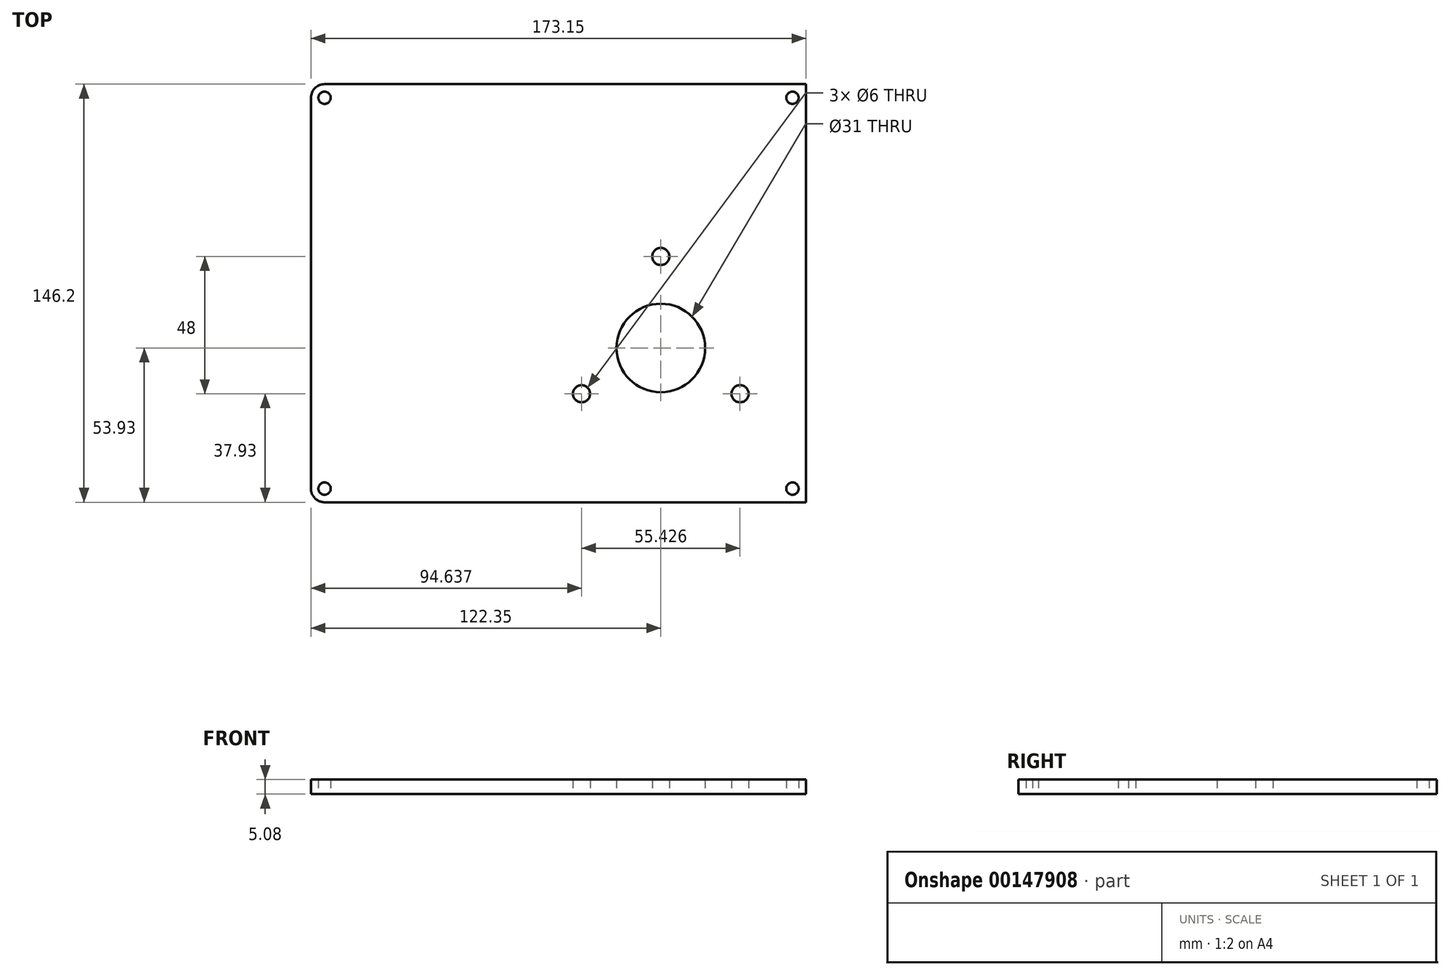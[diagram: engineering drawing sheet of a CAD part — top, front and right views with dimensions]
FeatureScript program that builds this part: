
annotation { "Feature Type Name" : "Feature", "Feature Type Description" : "" }
export const myFeature = defineFeature(function(context is Context, id is Id, definition is map)
    precondition{}
    {
        {
            var Q0;
            Q0=qCreatedBy(makeId("Top.planeOp"),FACE);
            var sketch = newSketch(context, id + "F0", { "sketchPlane" : qUnion([Q0])});
            skLineSegment(sketch, "E0", {"start": v(0, 0) * mm, "end": v(0, 32) * mm, "construction": true});
            skLineSegment(sketch, "E1", {"start": v(0, 0) * mm, "end": v(27.71, -16) * mm, "construction": true});
            skLineSegment(sketch, "E2", {"start": v(0, 0) * mm, "end": v(-27.71, -16) * mm, "construction": true});
            skLineSegment(sketch, "E3", {"start": v(0, 32) * mm, "end": v(27.71, -16) * mm, "construction": true});
            skLineSegment(sketch, "E4", {"start": v(27.71, -16) * mm, "end": v(-27.71, -16) * mm, "construction": true});
            skLineSegment(sketch, "E5", {"start": v(-27.71, -16) * mm, "end": v(0, 32) * mm, "construction": true});
            skCircle(sketch, "E6", {"center": v(0, 0) * mm, "radius": 15.5 * mm});
            skCircle(sketch, "E7", {"center": v(0, 32) * mm, "radius": 3 * mm});
            skCircle(sketch, "E8", {"center": v(-27.71, -16) * mm, "radius": 3 * mm});
            skCircle(sketch, "E9", {"center": v(27.71, -16) * mm, "radius": 3 * mm});
            skLineSegment(sketch, "E10.bottom", {"start": v(-117.58, 92.27) * mm, "end": v(50.8, 92.27) * mm});
            skLineSegment(sketch, "E10.top", {"start": v(-117.58, -53.93) * mm, "end": v(50.8, -53.93) * mm});
            skLineSegment(sketch, "E10.right", {"start": v(50.8, 92.27) * mm, "end": v(50.8, -53.93) * mm});
            skLineSegment(sketch, "E11", {"start": v(50.8, -49.17) * mm, "end": v(46.04, -49.17) * mm, "construction": true});
            skLineSegment(sketch, "E12", {"start": v(46.04, -49.17) * mm, "end": v(46.04, -53.93) * mm, "construction": true});
            skLineSegment(sketch, "E13", {"start": v(50.8, 87.51) * mm, "end": v(46.04, 87.51) * mm, "construction": true});
            skLineSegment(sketch, "E14", {"start": v(46.04, 87.51) * mm, "end": v(46.04, 92.27) * mm, "construction": true});
            skCircle(sketch, "E15", {"center": v(46.04, 87.51) * mm, "radius": 2.15 * mm});
            skCircle(sketch, "E16", {"center": v(46.04, -49.17) * mm, "radius": 2.15 * mm});
            skArc(sketch, "E17", {"start": v(-117.58, 92.27) * mm, "mid": v(-120.95, 90.88) * mm, "end": v(-122.35, 87.51) * mm});
            skArc(sketch, "E18", {"start": v(-122.35, -49.06) * mm, "mid": v(-121, -52.5) * mm, "end": v(-117.58, -53.93) * mm});
            skLineSegment(sketch, "E19", {"start": v(-122.35, 87.51) * mm, "end": v(-122.35, -49.06) * mm});
            skLineSegment(sketch, "E20", {"start": v(46.04, 87.51) * mm, "end": v(-117.58, 87.51) * mm, "construction": true});
            skLineSegment(sketch, "E21", {"start": v(46.04, -49.17) * mm, "end": v(-117.58, -49.17) * mm, "construction": true});
            skCircle(sketch, "E22", {"center": v(-117.58, 87.51) * mm, "radius": 2.15 * mm});
            skCircle(sketch, "E23", {"center": v(-117.58, -49.17) * mm, "radius": 2.15 * mm});
            skSolve(sketch);
        }
        {
            var Q0;
            Q0=qSketchRegion(id+"F0",true);
            extrude(context, id + "F1", {"entities" : qUnion([Q0]), "depth" : 5.08 * mm});
        }
    });
